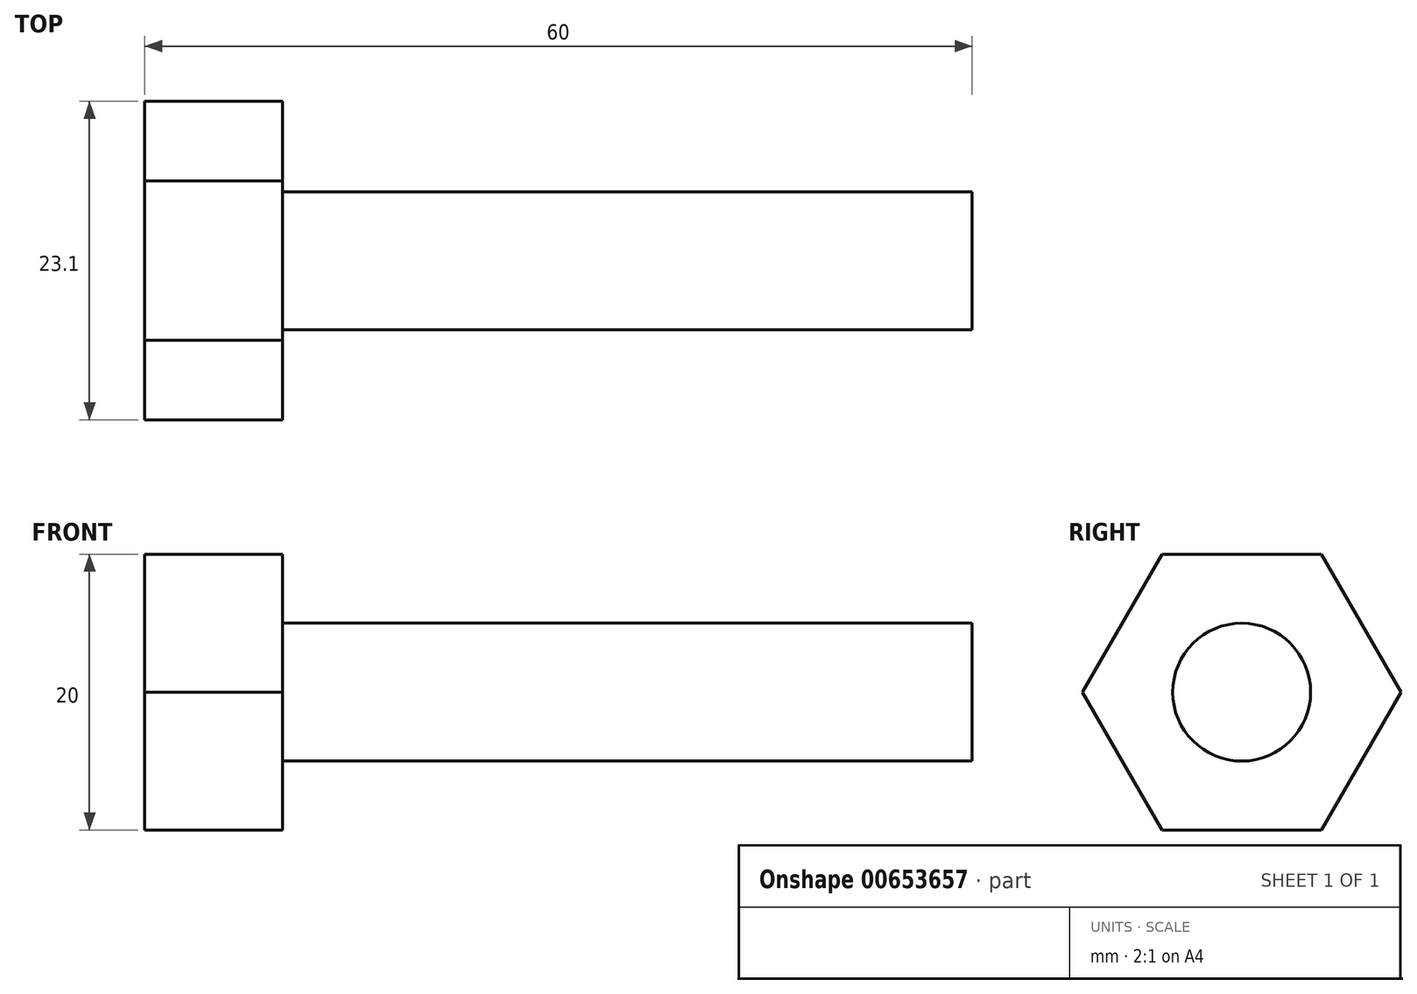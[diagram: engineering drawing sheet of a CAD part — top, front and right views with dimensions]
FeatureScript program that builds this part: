
annotation { "Feature Type Name" : "Feature", "Feature Type Description" : "" }
export const myFeature = defineFeature(function(context is Context, id is Id, definition is map)
    precondition{}
    {
        {
            var Q0;
            Q0=qCreatedBy(makeId("Right.planeOp"),FACE);
            var sketch = newSketch(context, id + "F0", { "sketchPlane" : qUnion([Q0])});
            skCircle(sketch, "E0.cCircle", {"center": v(0, 0) * mm, "radius": 10 * mm, "construction": true});
            skLineSegment(sketch, "E0.0", {"start": v(-5.77, 10) * mm, "end": v(5.77, 10) * mm});
            skLineSegment(sketch, "E0.1", {"start": v(5.77, 10) * mm, "end": v(11.55, 0) * mm});
            skLineSegment(sketch, "E0.2", {"start": v(11.55, 0) * mm, "end": v(5.77, -10) * mm});
            skLineSegment(sketch, "E0.3", {"start": v(5.77, -10) * mm, "end": v(-5.77, -10) * mm});
            skLineSegment(sketch, "E0.4", {"start": v(-5.77, -10) * mm, "end": v(-11.55, 0) * mm});
            skLineSegment(sketch, "E0.5", {"start": v(-11.55, 0) * mm, "end": v(-5.77, 10) * mm});
            skPoint(sketch, "E0.0.midPoint", {"position": v(0, 10) * mm});
            skSolve(sketch);
        }
        {
            var Q0;
            Q0 = qSketchRegion(id + "F0", true);
            extrude(context, id + "F1", {"entities" : qUnion([Q0]), "depth" : 10 * mm, "offsetDistance" : 25 * mm});
        }
        {
            var Q0;
            Q0=makeQuery(id+"F1.opExtrude","CAP_FACE",FACE,{"disambiguationData":[OSD([sQuery(id+"F0.wireOp",EDGE,"E0.0"),sQuery(id+"F0.wireOp",EDGE,"E0.1"),sQuery(id+"F0.wireOp",EDGE,"E0.2"),sQuery(id+"F0.wireOp",EDGE,"E0.3"),sQuery(id+"F0.wireOp",EDGE,"E0.4"),sQuery(id+"F0.wireOp",EDGE,"E0.5")])],"isStart":false});
            var sketch = newSketch(context, id + "F2", { "sketchPlane" : qUnion([Q0])});
            skCircle(sketch, "E1", {"center": v(0, 0) * mm, "radius": 5 * mm});
            skSolve(sketch);
        }
        {
            var Q0;
            Q0=makeQuery(id+"F2.imprint","IMPRINT",FACE,{"disambiguationData":[TD([[makeQuery(id+"F2.imprint","IMPRINT",EDGE,{"derivedFrom":sQuery(id+"F2.wireOp",EDGE,"E1")}),1.0]])]});
            extrude(context, id + "F3", {"entities" : qUnion([Q0]), "operationType" : NewBodyOperationType.ADD, "depth" : 50 * mm, "offsetDistance" : 25 * mm});
        }
    });
